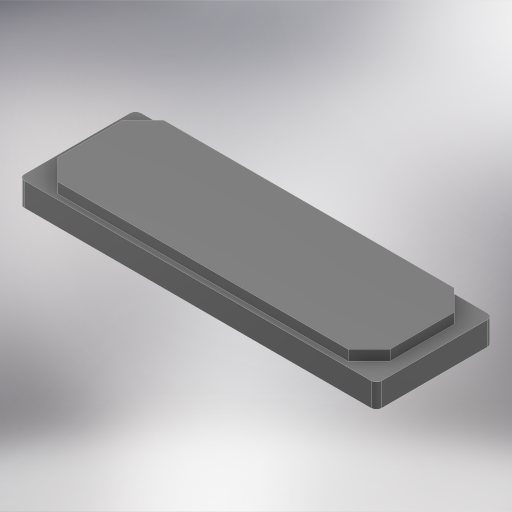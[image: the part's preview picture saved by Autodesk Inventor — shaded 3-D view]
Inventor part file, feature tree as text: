
AUTODESK INVENTOR PART (.ipt)
format: ipt  version: 2024 (Build 280153000, 153)  size: 333,824 bytes
history: native  units: mm
features: extrude x3, sketch x3, fillet x2, chamfer x1, projected_geometry x1
ambient origin geometry x8: Origin, YZ Plane, XZ Plane, XY Plane, X Axis, Y Axis, Z Axis, Center Point
bodies: Solid1 (feature_tree)
feature tree (10):
  extrude  "Extrusion1"  Depth=11.1mm
  extrude  "Extrusion2"  Depth=1.2mm
  extrude  "Extrusion3"  Depth=0.5mm
  fillet  "Fillet1"  Radius=0.5mm
  fillet  "Fillet2"  Radius=1.0mm
  chamfer  "Chamfer1"  Distance=32.9mm
  sketch  "Sketch1"  dims[d0=34.0mm d1=11.1mm]
  sketch  "Sketch2"  dims[d2=3.5mm d3=0.0mm d4=1.2mm]
  sketch  "Sketch3"  dims[d5=1.2mm d6=0.5mm d7=0.5mm d8=1.0mm d9=0.0mm d10=32.9mm d11=9.9mm d12=0.25mm d13=0.0mm d14=2.0mm d15=0.5mm d16=2.0mm d17=2.0mm d18=45.0deg]
  projected_geometry  "Projected Loop1"
